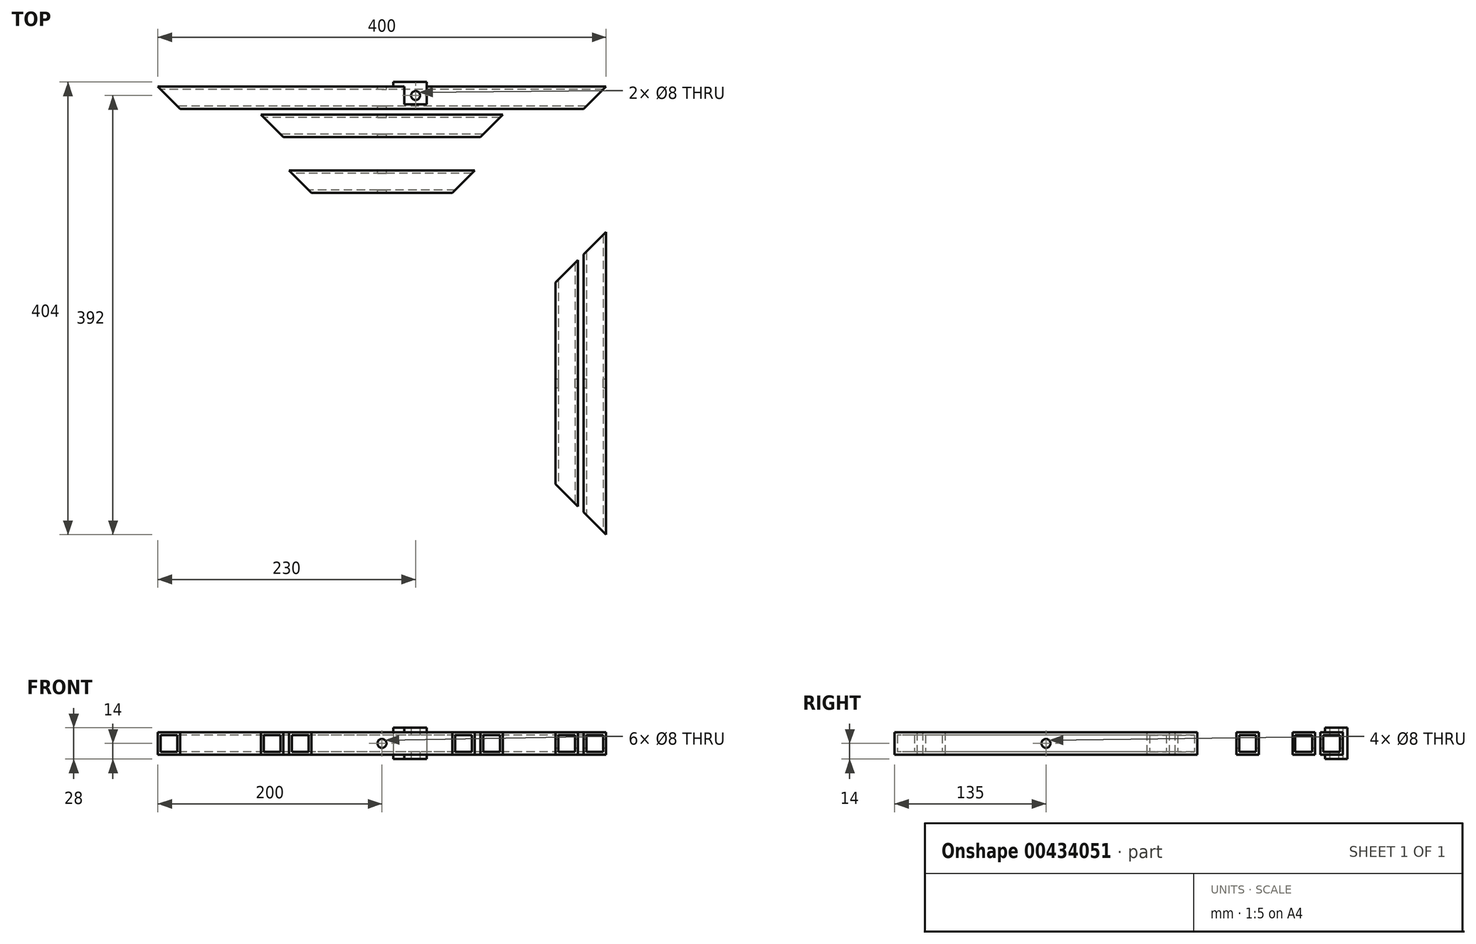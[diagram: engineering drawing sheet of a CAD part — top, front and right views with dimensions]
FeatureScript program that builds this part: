
annotation { "Feature Type Name" : "Feature", "Feature Type Description" : "" }
export const myFeature = defineFeature(function(context is Context, id is Id, definition is map)
    precondition{}
    {
        {
            var Q0;
            Q0=qCreatedBy(makeId("Top.planeOp"),FACE);
            var sketch = newSketch(context, id + "F0", { "sketchPlane" : qUnion([Q0])});
            skLineSegment(sketch, "E0.bottom", {"start": v(200, 200) * mm, "end": v(-200, 200) * mm});
            skLineSegment(sketch, "E0.top", {"start": v(200, -200) * mm, "end": v(-200, -200) * mm});
            skLineSegment(sketch, "E0.left", {"start": v(200, 200) * mm, "end": v(200, -200) * mm});
            skLineSegment(sketch, "E0.right", {"start": v(-200, 200) * mm, "end": v(-200, -200) * mm});
            skPoint(sketch, "E0.middle", {"position": v(0, 0) * mm});
            skLineSegment(sketch, "E1.0", {"start": v(180, 180) * mm, "end": v(-180, 180) * mm});
            skLineSegment(sketch, "E1.1", {"start": v(180, 180) * mm, "end": v(180, -180) * mm});
            skLineSegment(sketch, "E1.2", {"start": v(180, -180) * mm, "end": v(-180, -180) * mm});
            skLineSegment(sketch, "E1.3", {"start": v(-180, 180) * mm, "end": v(-180, -180) * mm});
            skLineSegment(sketch, "E2.0", {"start": v(175, 175) * mm, "end": v(175, -175) * mm, "construction": true});
            skLineSegment(sketch, "E2.1", {"start": v(175, 175) * mm, "end": v(-175, 175) * mm});
            skLineSegment(sketch, "E2.2", {"start": v(-175, 175) * mm, "end": v(-175, -175) * mm});
            skLineSegment(sketch, "E2.3", {"start": v(175, -175) * mm, "end": v(-175, -175) * mm});
            skLineSegment(sketch, "E3.0", {"start": v(-155, 155) * mm, "end": v(-155, -155) * mm});
            skLineSegment(sketch, "E3.1", {"start": v(155, 155) * mm, "end": v(-155, 155) * mm});
            skLineSegment(sketch, "E3.2", {"start": v(155, 155) * mm, "end": v(155, -155) * mm});
            skLineSegment(sketch, "E3.3", {"start": v(155, -155) * mm, "end": v(-155, -155) * mm});
            skLineSegment(sketch, "E4", {"start": v(-200, 200) * mm, "end": v(-180, 180) * mm});
            skLineSegment(sketch, "E5", {"start": v(-175, 175) * mm, "end": v(-155, 155) * mm});
            skLineSegment(sketch, "E6", {"start": v(155, 155) * mm, "end": v(175, 175) * mm});
            skLineSegment(sketch, "E7", {"start": v(180, 180) * mm, "end": v(200, 200) * mm});
            skLineSegment(sketch, "E8", {"start": v(180, -180) * mm, "end": v(200, -200) * mm});
            skLineSegment(sketch, "E9", {"start": v(180, 50) * mm, "end": v(200, 70) * mm});
            skLineSegment(sketch, "E10", {"start": v(155, 25) * mm, "end": v(175, 45) * mm});
            skLineSegment(sketch, "E11", {"start": v(155, -155) * mm, "end": v(175, -175) * mm});
            skLineSegment(sketch, "E12.bottom", {"start": v(82.92, 125) * mm, "end": v(-82.92, 125) * mm});
            skLineSegment(sketch, "E12.top", {"start": v(82.92, -125) * mm, "end": v(-82.92, -125) * mm});
            skLineSegment(sketch, "E12.left", {"start": v(82.92, 125) * mm, "end": v(82.92, -125) * mm});
            skLineSegment(sketch, "E12.right", {"start": v(-82.92, 125) * mm, "end": v(-82.92, -125) * mm});
            skLineSegment(sketch, "E13.0", {"start": v(62.92, 105) * mm, "end": v(-62.92, 105) * mm});
            skLineSegment(sketch, "E13.1", {"start": v(62.92, 105) * mm, "end": v(62.92, -105) * mm});
            skLineSegment(sketch, "E13.2", {"start": v(62.92, -105) * mm, "end": v(-62.92, -105) * mm});
            skLineSegment(sketch, "E13.3", {"start": v(-62.92, 105) * mm, "end": v(-62.92, -105) * mm});
            skLineSegment(sketch, "E14", {"start": v(-82.92, 125) * mm, "end": v(-62.92, 105) * mm});
            skLineSegment(sketch, "E15", {"start": v(82.92, 125) * mm, "end": v(62.92, 105) * mm});
            skLineSegment(sketch, "E16", {"start": v(175, 45) * mm, "end": v(175, -175) * mm});
            skLineSegment(sketch, "E17", {"start": v(-107.92, 175) * mm, "end": v(-87.92, 155) * mm});
            skLineSegment(sketch, "E18", {"start": v(107.92, 175) * mm, "end": v(87.92, 155) * mm});
            skLineSegment(sketch, "E19", {"start": v(0, 2.72) * mm, "end": v(0, 200) * mm, "construction": true});
            skSolve(sketch);
        }
        {
            var Q0;
            {var subQ0=sQuery(id+"F0.wireOp",EDGE,"E17");Q0=makeQuery(id+"F0.imprint","IMPRINT",FACE,{"disambiguationData":[TD([[makeQuery(id+"F0.imprint","IMPRINT",EDGE,{"derivedFrom":subQ0}),1.0]])]});}
            var Q1;
            Q1=makeQuery(id+"F0.imprint","IMPRINT",FACE,{"disambiguationData":[TD([[makeQuery(id+"F0.imprint","IMPRINT",EDGE,{"derivedFrom":sQuery(id+"F0.wireOp",EDGE,"E0.bottom")}),1.0]])]});
            var Q2;
            {var subQ2=sQuery(id+"F0.wireOp",EDGE,"E10");Q2=makeQuery(id+"F0.imprint","IMPRINT",FACE,{"disambiguationData":[TD([[makeQuery(id+"F0.imprint","IMPRINT",EDGE,{"derivedFrom":subQ2}),-1.0]])]});}
            var Q3;
            {var subQ0=sQuery(id+"F0.wireOp",EDGE,"E8");Q3=makeQuery(id+"F0.imprint","IMPRINT",FACE,{"disambiguationData":[TD([[makeQuery(id+"F0.imprint","IMPRINT",EDGE,{"derivedFrom":subQ0}),1.0]])]});}
            var Q4;
            Q4=makeQuery(id+"F0.imprint","IMPRINT",FACE,{"disambiguationData":[TD([[makeQuery(id+"F0.imprint","IMPRINT",EDGE,{"derivedFrom":sQuery(id+"F0.wireOp",EDGE,"E12.bottom")}),1.0]])]});
            extrude(context, id + "F1", {"entities" : qUnion([Q0, Q1, Q2, Q3, Q4]), "depth" : 20 * mm});
        }
        {
            var Q0;
            Q0=makeQuery(id+"F1.opExtrude","SWEPT_FACE",FACE,{"disambiguationData":[OSD([sQuery(id+"F0.wireOp",EDGE,"E7")])]});
            var Q1;
            Q1=makeQuery(id+"F1.opExtrude","SWEPT_FACE",FACE,{"disambiguationData":[OSD([sQuery(id+"F0.wireOp",EDGE,"E6")])]});
            var Q2;
            Q2=makeQuery(id+"F1.opExtrude","SWEPT_FACE",FACE,{"disambiguationData":[OSD([sQuery(id+"F0.wireOp",EDGE,"E5")])]});
            var Q3;
            Q3=makeQuery(id+"F1.opExtrude","SWEPT_FACE",FACE,{"disambiguationData":[OSD([sQuery(id+"F0.wireOp",EDGE,"E4")])]});
            var Q4;
            Q4=makeQuery(id+"F1.opExtrude","SWEPT_FACE",FACE,{"disambiguationData":[OSD([sQuery(id+"F0.wireOp",EDGE,"E10")])]});
            var Q5;
            Q5=makeQuery(id+"F1.opExtrude","SWEPT_FACE",FACE,{"disambiguationData":[OSD([sQuery(id+"F0.wireOp",EDGE,"E9")])]});
            var Q6;
            Q6=makeQuery(id+"F1.opExtrude","SWEPT_FACE",FACE,{"disambiguationData":[OSD([sQuery(id+"F0.wireOp",EDGE,"E11")])]});
            var Q7;
            Q7=makeQuery(id+"F1.opExtrude","SWEPT_FACE",FACE,{"disambiguationData":[OSD([sQuery(id+"F0.wireOp",EDGE,"E8")])]});
            var Q8;
            Q8=makeQuery(id+"F1.opExtrude","SWEPT_FACE",FACE,{"disambiguationData":[OSD([sQuery(id+"F0.wireOp",EDGE,"E14")])]});
            var Q9;
            Q9=makeQuery(id+"F1.opExtrude","SWEPT_FACE",FACE,{"disambiguationData":[OSD([sQuery(id+"F0.wireOp",EDGE,"E15")])]});
            var Q10;
            Q10=makeQuery(id+"F1.opExtrude","SWEPT_FACE",FACE,{"disambiguationData":[OSD([sQuery(id+"F0.wireOp",EDGE,"E17")])]});
            var Q11;
            Q11=makeQuery(id+"F1.opExtrude","SWEPT_FACE",FACE,{"disambiguationData":[OSD([sQuery(id+"F0.wireOp",EDGE,"E18")])]});
            shell(context, id + "F2", {"entities" : qUnion([Q0, Q1, Q2, Q3, Q4, Q5, Q6, Q7, Q8, Q9, Q10, Q11]), "thickness" : 2.5 * mm});
        }
        {
            var Q0;
            Q0=makeQuery(id+"F1.opExtrude","SWEPT_FACE",FACE,{"disambiguationData":[OSD([sQuery(id+"F0.wireOp",EDGE,"E0.bottom")])]});
            var sketch = newSketch(context, id + "F3", { "sketchPlane" : qUnion([Q0])});
            skCircle(sketch, "E20", {"center": v(0, 10) * mm, "radius": 4 * mm});
            skSolve(sketch);
        }
        {
            var Q0;
            Q0=makeQuery(id+"F1.opExtrude","SWEPT_FACE",FACE,{"disambiguationData":[OSD([sQuery(id+"F0.wireOp",EDGE,"E0.left")])]});
            var sketch = newSketch(context, id + "F4", { "sketchPlane" : qUnion([Q0])});
            skCircle(sketch, "E21", {"center": v(-65, 10) * mm, "radius": 4 * mm});
            skPoint(sketch, "E21.centerSnap0", {"position": v(-65, 20) * mm});
            skSolve(sketch);
        }
        {
            var Q0;
            Q0 = qSketchRegion(id + "F3", true);
            extrude(context, id + "F5", {"entities" : qUnion([Q0]), "operationType" : NewBodyOperationType.REMOVE, "endBound" : BoundingType.THROUGH_ALL, "oppositeDirection" : true, "depth" : 25 * mm});
        }
        {
            var Q0;
            Q0 = qSketchRegion(id + "F4", true);
            extrude(context, id + "F6", {"entities" : qUnion([Q0]), "operationType" : NewBodyOperationType.REMOVE, "endBound" : BoundingType.THROUGH_ALL, "oppositeDirection" : true, "depth" : 25 * mm});
        }
        {
            var Q0;
            Q0=makeQuery(id+"F1.opExtrude","SWEPT_FACE",FACE,{"disambiguationData":[OSD([sQuery(id+"F0.wireOp",EDGE,"E0.bottom")])]});
            var sketch = newSketch(context, id + "F7", { "sketchPlane" : qUnion([Q0])});
            skLineSegment(sketch, "E22.bottom", {"start": v(-20, 20) * mm, "end": v(-40, 20) * mm});
            skLineSegment(sketch, "E22.top", {"start": v(-20, 0) * mm, "end": v(-40, 0) * mm});
            skLineSegment(sketch, "E22.left", {"start": v(-20, 20) * mm, "end": v(-20, 0) * mm});
            skLineSegment(sketch, "E22.right", {"start": v(-40, 20) * mm, "end": v(-40, 0) * mm});
            skSolve(sketch);
        }
        {
            var Q0;
            Q0 = qSketchRegion(id + "F7", true);
            extrude(context, id + "F8", {"entities" : qUnion([Q0]), "depth" : 4 * mm});
        }
        {
            var Q0;
            Q0=makeQuery(id+"F8.opExtrude","CAP_FACE",FACE,{"disambiguationData":[OSD([sQuery(id+"F7.wireOp",EDGE,"E22.bottom"),sQuery(id+"F7.wireOp",EDGE,"E22.top"),sQuery(id+"F7.wireOp",EDGE,"E22.left"),sQuery(id+"F7.wireOp",EDGE,"E22.right")])],"isStart":false});
            var sketch = newSketch(context, id + "F9", { "sketchPlane" : qUnion([Q0])});
            skLineSegment(sketch, "E23.bottom", {"start": v(-20, 0) * mm, "end": v(-40, 0) * mm});
            skLineSegment(sketch, "E23.top", {"start": v(-20, -4) * mm, "end": v(-40, -4) * mm});
            skLineSegment(sketch, "E23.left", {"start": v(-20, 0) * mm, "end": v(-20, -4) * mm});
            skLineSegment(sketch, "E23.right", {"start": v(-40, 0) * mm, "end": v(-40, -4) * mm});
            skLineSegment(sketch, "E24.bottom", {"start": v(-20, 20) * mm, "end": v(-40, 20) * mm});
            skLineSegment(sketch, "E24.top", {"start": v(-20, 24) * mm, "end": v(-40, 24) * mm});
            skLineSegment(sketch, "E24.left", {"start": v(-20, 20) * mm, "end": v(-20, 24) * mm});
            skLineSegment(sketch, "E24.right", {"start": v(-40, 20) * mm, "end": v(-40, 24) * mm});
            skSolve(sketch);
        }
        {
            var Q0;
            Q0 = qSketchRegion(id + "F9", true);
            extrude(context, id + "F10", {"entities" : qUnion([Q0]), "operationType" : NewBodyOperationType.ADD, "oppositeDirection" : true, "depth" : 20 * mm});
        }
        {
            var Q0;
            Q0=makeQuery(id+"F10.opExtrude","SWEPT_FACE",FACE,{"disambiguationData":[OSD([sQuery(id+"F9.wireOp",EDGE,"E23.top")])]});
            var sketch = newSketch(context, id + "F11", { "sketchPlane" : qUnion([Q0])});
            skCircle(sketch, "E25", {"center": v(30, -192) * mm, "radius": 4 * mm});
            skPoint(sketch, "E25.centerSnap0", {"position": v(30, -184) * mm});
            skSolve(sketch);
        }
        {
            var Q0;
            Q0 = qSketchRegion(id + "F11", true);
            extrude(context, id + "F12", {"entities" : qUnion([Q0]), "operationType" : NewBodyOperationType.REMOVE, "endBound" : BoundingType.THROUGH_ALL, "oppositeDirection" : true, "depth" : 25 * mm});
        }
        {
            var Q0;
            Q0=makeQuery(id+"F10.boolean.opBoolean","MERGE",FACE,{"derivedFrom":[makeQuery(id+"F8.opExtrude","CAP_FACE",FACE,{"disambiguationData":[OSD([sQuery(id+"F7.wireOp",EDGE,"E22.bottom"),sQuery(id+"F7.wireOp",EDGE,"E22.top"),sQuery(id+"F7.wireOp",EDGE,"E22.left"),sQuery(id+"F7.wireOp",EDGE,"E22.right")])],"isStart":false}),makeQuery(id+"F10.opExtrude","CAP_FACE",FACE,{"disambiguationData":[OSD([sQuery(id+"F9.wireOp",EDGE,"E23.bottom"),sQuery(id+"F9.wireOp",EDGE,"E23.top"),sQuery(id+"F9.wireOp",EDGE,"E23.left"),sQuery(id+"F9.wireOp",EDGE,"E23.right")])],"isStart":true}),makeQuery(id+"F10.opExtrude","CAP_FACE",FACE,{"disambiguationData":[OSD([sQuery(id+"F9.wireOp",EDGE,"E24.bottom"),sQuery(id+"F9.wireOp",EDGE,"E24.top"),sQuery(id+"F9.wireOp",EDGE,"E24.left"),sQuery(id+"F9.wireOp",EDGE,"E24.right")])],"isStart":true})]});
            var sketch = newSketch(context, id + "F13", { "sketchPlane" : qUnion([Q0])});
            skLineSegment(sketch, "E26.bottom", {"start": v(-20, 24) * mm, "end": v(-10, 24) * mm});
            skLineSegment(sketch, "E26.top", {"start": v(-20, -4) * mm, "end": v(-10, -4) * mm});
            skLineSegment(sketch, "E26.left", {"start": v(-20, 24) * mm, "end": v(-20, -4) * mm});
            skLineSegment(sketch, "E26.right", {"start": v(-10, 24) * mm, "end": v(-10, -4) * mm});
            skSolve(sketch);
        }
        {
            var Q0;
            Q0 = qSketchRegion(id + "F13", true);
            extrude(context, id + "F14", {"entities" : qUnion([Q0]), "operationType" : NewBodyOperationType.ADD, "oppositeDirection" : true, "depth" : 4 * mm});
        }
    });
